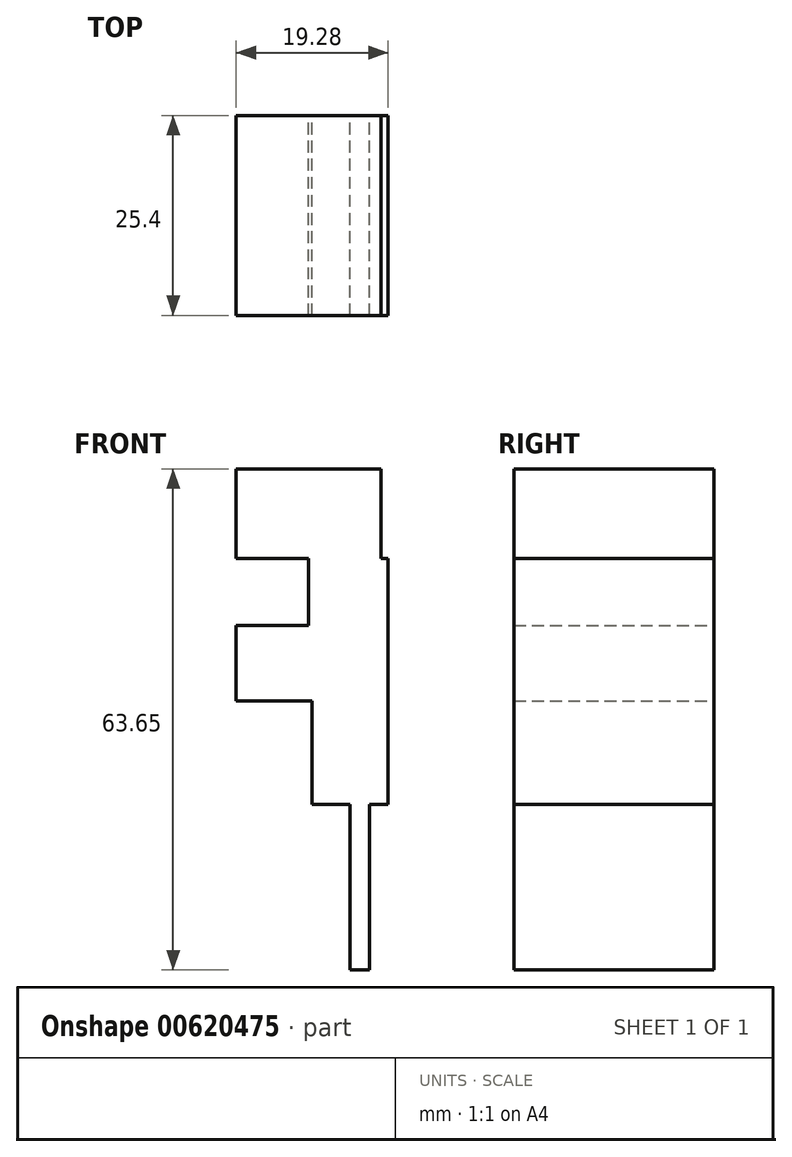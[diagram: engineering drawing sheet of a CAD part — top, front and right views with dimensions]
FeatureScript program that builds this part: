
annotation { "Feature Type Name" : "Feature", "Feature Type Description" : "" }
export const myFeature = defineFeature(function(context is Context, id is Id, definition is map)
    precondition{}
    {
        {
            var Q0;
            Q0=qCreatedBy(makeId("Front.planeOp"),FACE);
            var sketch = newSketch(context, id + "F0", { "sketchPlane" : qUnion([Q0])});
            skLineSegment(sketch, "E0.bottom", {"start": v(-19.71, 15.91) * mm, "end": v(-38.1, 15.91) * mm});
            skLineSegment(sketch, "E0.top", {"start": v(-19.71, 4.53) * mm, "end": v(-38.1, 4.53) * mm});
            skLineSegment(sketch, "E0.left", {"start": v(-19.71, 15.91) * mm, "end": v(-19.71, 4.53) * mm});
            skLineSegment(sketch, "E0.right", {"start": v(-38.1, 15.91) * mm, "end": v(-38.1, 4.53) * mm});
            skLineSegment(sketch, "E1.bottom", {"start": v(-28.9, 4.53) * mm, "end": v(-18.83, 4.53) * mm});
            skLineSegment(sketch, "E1.top", {"start": v(-28.9, -3.94) * mm, "end": v(-18.83, -3.94) * mm});
            skLineSegment(sketch, "E1.left", {"start": v(-28.9, 4.53) * mm, "end": v(-28.9, -3.94) * mm});
            skLineSegment(sketch, "E1.right", {"start": v(-18.83, 4.53) * mm, "end": v(-18.83, -3.94) * mm});
            skPoint(sketch, "E2.firstSnap0", {"position": v(-23.87, -3.94) * mm});
            skLineSegment(sketch, "E2.bottom", {"start": v(-38.1, -3.94) * mm, "end": v(-18.83, -3.94) * mm});
            skLineSegment(sketch, "E2.top", {"start": v(-38.1, -13.58) * mm, "end": v(-18.83, -13.58) * mm});
            skLineSegment(sketch, "E2.left", {"start": v(-38.1, -3.94) * mm, "end": v(-38.1, -13.58) * mm});
            skLineSegment(sketch, "E2.right", {"start": v(-18.83, -3.94) * mm, "end": v(-18.83, -13.58) * mm});
            skLineSegment(sketch, "E3.bottom", {"start": v(-28.47, -13.58) * mm, "end": v(-18.83, -13.58) * mm});
            skLineSegment(sketch, "E3.top", {"start": v(-28.47, -26.72) * mm, "end": v(-18.83, -26.72) * mm});
            skLineSegment(sketch, "E3.left", {"start": v(-28.47, -13.58) * mm, "end": v(-28.47, -26.72) * mm});
            skLineSegment(sketch, "E3.right", {"start": v(-18.83, -13.58) * mm, "end": v(-18.83, -26.72) * mm});
            skLineSegment(sketch, "E4.bottom", {"start": v(-23.65, -26.72) * mm, "end": v(-21.17, -26.72) * mm});
            skLineSegment(sketch, "E4.top", {"start": v(-23.65, -47.74) * mm, "end": v(-21.17, -47.74) * mm});
            skLineSegment(sketch, "E4.left", {"start": v(-23.65, -26.72) * mm, "end": v(-23.65, -47.74) * mm});
            skLineSegment(sketch, "E4.right", {"start": v(-21.17, -26.72) * mm, "end": v(-21.17, -47.74) * mm});
            skSolve(sketch);
        }
        {
            var Q0;
            Q0 = qSketchRegion(id + "F0", true);
            extrude(context, id + "F1", {"entities" : qUnion([Q0]), "depth" : 25.4 * mm, "offsetDistance" : 25.4 * mm});
        }
    });
